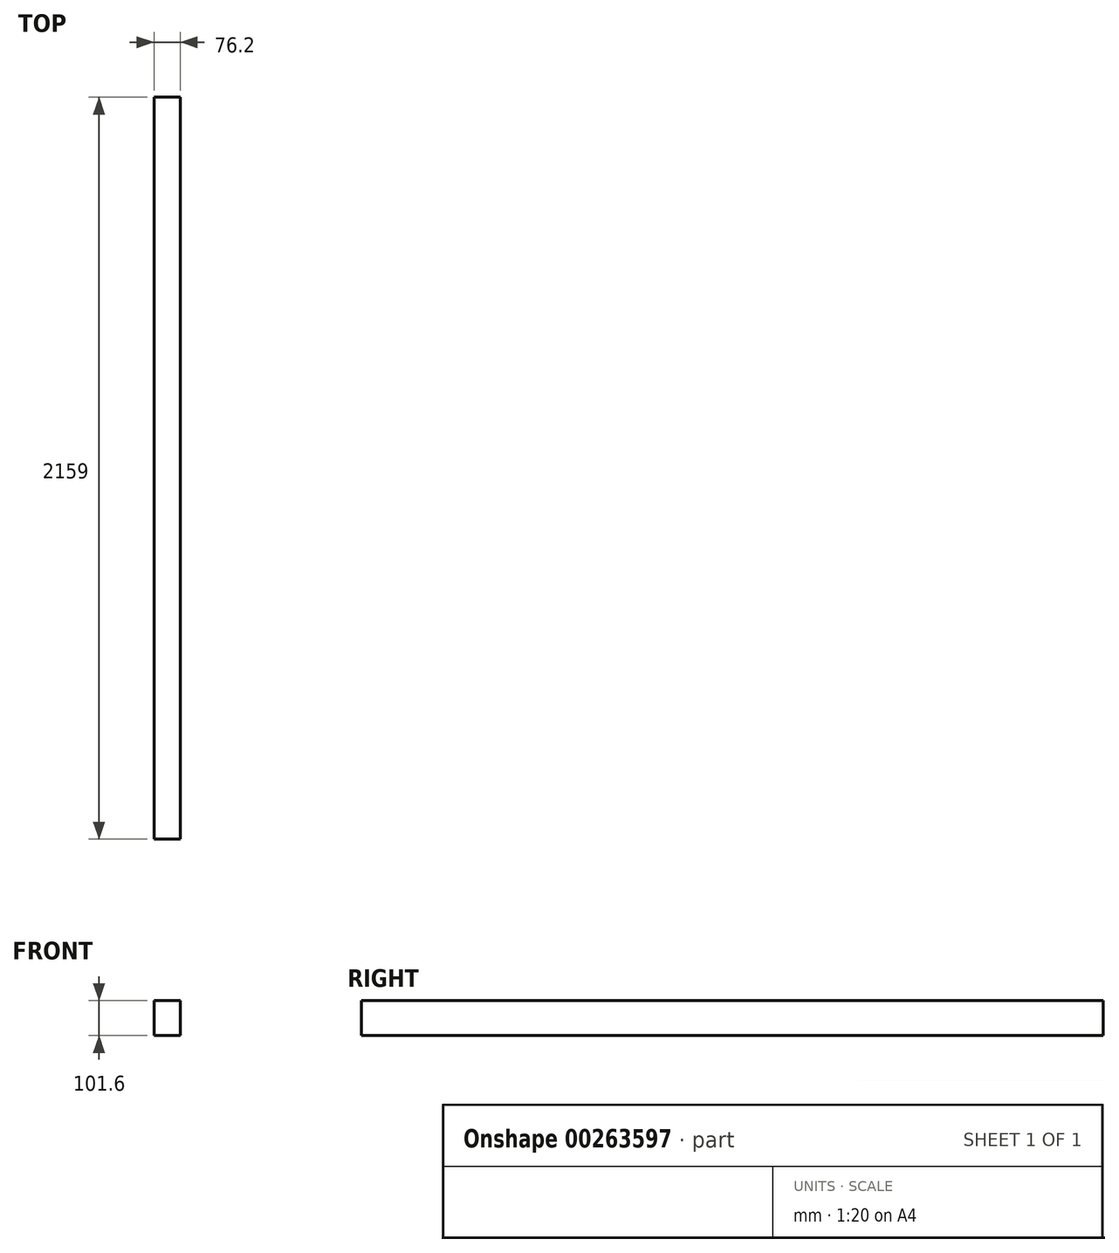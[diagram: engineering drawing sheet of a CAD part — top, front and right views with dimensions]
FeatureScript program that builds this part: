
annotation { "Feature Type Name" : "Feature", "Feature Type Description" : "" }
export const myFeature = defineFeature(function(context is Context, id is Id, definition is map)
    precondition{}
    {
        {
            var Q0;
            Q0=qCreatedBy(makeId("Front.planeOp"),FACE);
            var sketch = newSketch(context, id + "F0", { "sketchPlane" : qUnion([Q0])});
            skLineSegment(sketch, "E0.bottom", {"start": v(0, 0) * mm, "end": v(76.2, 0) * mm});
            skLineSegment(sketch, "E0.top", {"start": v(0, 101.6) * mm, "end": v(76.2, 101.6) * mm});
            skLineSegment(sketch, "E0.left", {"start": v(0, 0) * mm, "end": v(0, 101.6) * mm});
            skLineSegment(sketch, "E0.right", {"start": v(76.2, 0) * mm, "end": v(76.2, 101.6) * mm});
            skSolve(sketch);
        }
        {
            var Q0;
            Q0=makeQuery(id+"F0.imprint","IMPRINT",FACE,{"disambiguationData":[TD([[makeQuery(id+"F0.imprint","IMPRINT",EDGE,{"derivedFrom":sQuery(id+"F0.wireOp",EDGE,"E0.bottom")}),1.0]])]});
            extrude(context, id + "F1", {"entities" : qUnion([Q0]), "depth" : 2159 * mm});
        }
        {
            var Q0;
            Q0=makeQuery(id+"F1.opExtrude","SWEPT_FACE",FACE,{"disambiguationData":[OSD([sQuery(id+"F0.wireOp",EDGE,"E0.left")])]});
            var sketch = newSketch(context, id + "F2", { "sketchPlane" : qUnion([Q0])});
            skCircle(sketch, "E1", {"center": v(452.85, 50.95) * mm, "radius": 36.97 * mm});
            skSolve(sketch);
        }
        {
            var Q0;
            Q0=sQuery(id+"F2.wireOp",EDGE,"E1");
            extrude(context, id + "F3", {"bodyType" : ToolBodyType.SURFACE, "surfaceEntities" : qUnion([Q0]), "depth" : 25.4 * mm});
        }
    });
